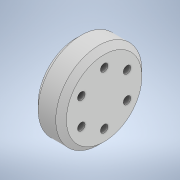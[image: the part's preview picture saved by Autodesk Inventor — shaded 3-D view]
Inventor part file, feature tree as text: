
AUTODESK INVENTOR PART (.ipt)
format: ipt  version: 2022 (Build 260153000, 153)  size: 177,152 bytes
history: native  units: mm
features: sketch x4, revolve x2, hole x2, other x1
ambient origin geometry x8: Origin, YZ Plane, XZ Plane, XY Plane, X Axis, Y Axis, Z Axis, Center Point
bodies: Body1 (feature_tree)
feature tree (9):
  other  "Твердое тело1"
  revolve  "Вращение1"
  hole  "Отверстие1"  [1 undecoded]
  hole  "Отверстие2"  [1 undecoded]
  revolve  "Вращение2"
  sketch  "Эскиз1"
  sketch  "Эскиз2"
  sketch  "Эскиз3"
  sketch  "Эскиз4"
note: 2 required parameter values undecoded (feature->parameter linkage not recoverable at this tier; creation-order binding heuristic only, values carry confidence <= 0.55)
